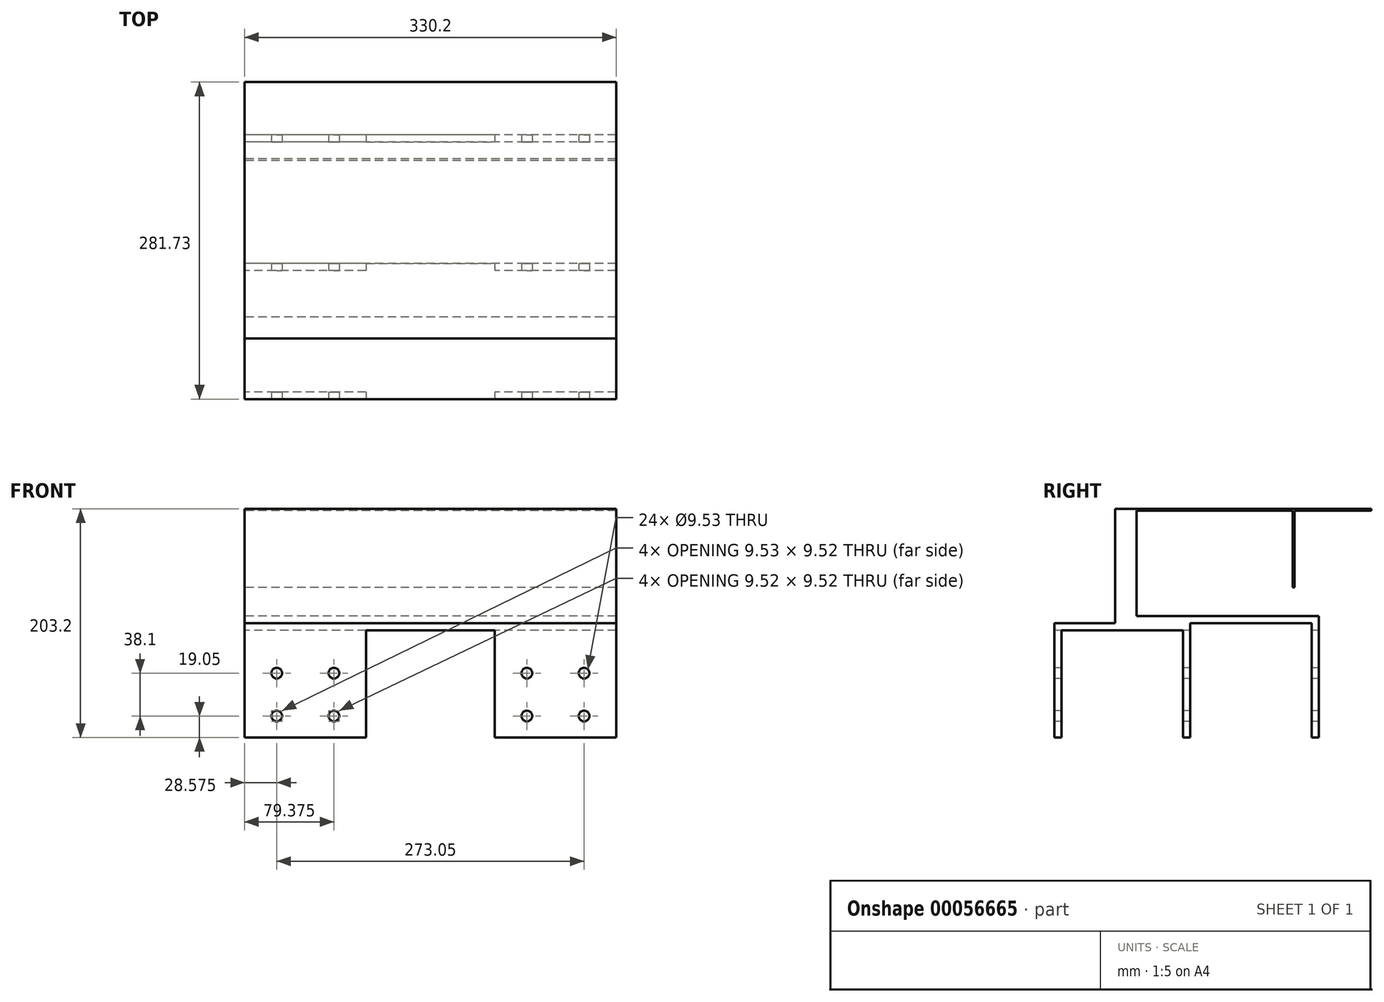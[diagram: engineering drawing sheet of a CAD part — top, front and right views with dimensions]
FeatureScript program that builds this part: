
annotation { "Feature Type Name" : "Feature", "Feature Type Description" : "" }
export const myFeature = defineFeature(function(context is Context, id is Id, definition is map)
    precondition{}
    {
        {
            var Q0;
            Q0=qCreatedBy(makeId("Right.planeOp"),FACE);
            var sketch = newSketch(context, id + "F0", { "sketchPlane" : qUnion([Q0])});
            skLineSegment(sketch, "E0", {"start": v(-73.02, -107.95) * mm, "end": v(-66.67, -107.95) * mm});
            skLineSegment(sketch, "E1", {"start": v(-66.67, -107.95) * mm, "end": v(-66.67, -12.7) * mm});
            skLineSegment(sketch, "E2", {"start": v(-66.67, -12.7) * mm, "end": v(-12.7, -12.7) * mm});
            skLineSegment(sketch, "E3", {"start": v(-12.7, -12.7) * mm, "end": v(-12.7, 95.25) * mm});
            skLineSegment(sketch, "E4", {"start": v(-73.02, -107.95) * mm, "end": v(-73.02, -6.35) * mm});
            skLineSegment(sketch, "E5", {"start": v(-12.7, 95.25) * mm, "end": v(-12.7, -12.7) * mm});
            skLineSegment(sketch, "E6", {"start": v(-12.7, -12.7) * mm, "end": v(41.28, -12.7) * mm});
            skLineSegment(sketch, "E7", {"start": v(41.28, -12.7) * mm, "end": v(41.28, -107.95) * mm});
            skLineSegment(sketch, "E8", {"start": v(41.28, -107.95) * mm, "end": v(47.63, -107.95) * mm});
            skLineSegment(sketch, "E9", {"start": v(47.63, -107.95) * mm, "end": v(47.63, -6.35) * mm});
            skLineSegment(sketch, "E10", {"start": v(47.63, -6.35) * mm, "end": v(-6.35, -6.35) * mm});
            skLineSegment(sketch, "E11", {"start": v(-6.35, -6.35) * mm, "end": v(-6.35, 95.25) * mm});
            skLineSegment(sketch, "E12", {"start": v(-6.35, 95.25) * mm, "end": v(-12.7, 95.25) * mm});
            skLineSegment(sketch, "E13", {"start": v(-19.05, 95.25) * mm, "end": v(-12.7, 95.25) * mm});
            skLineSegment(sketch, "E14", {"start": v(-73.02, -6.35) * mm, "end": v(-19.05, -6.35) * mm});
            skLineSegment(sketch, "E15", {"start": v(-19.05, -6.35) * mm, "end": v(-19.05, 95.25) * mm});
            skLineSegment(sketch, "E16", {"start": v(-6.35, 95.25) * mm, "end": v(0, 95.25) * mm});
            skLineSegment(sketch, "E17", {"start": v(0, 95.25) * mm, "end": v(0, 0) * mm});
            skLineSegment(sketch, "E18", {"start": v(0, 0) * mm, "end": v(161.93, 0) * mm});
            skLineSegment(sketch, "E19", {"start": v(161.93, 0) * mm, "end": v(161.93, -107.95) * mm});
            skLineSegment(sketch, "E20", {"start": v(161.93, -107.95) * mm, "end": v(155.58, -107.95) * mm});
            skLineSegment(sketch, "E21", {"start": v(155.58, -107.95) * mm, "end": v(155.58, -6.35) * mm});
            skLineSegment(sketch, "E22", {"start": v(155.58, -6.35) * mm, "end": v(47.63, -6.35) * mm});
            skLineSegment(sketch, "E23", {"start": v(138.85, 93.66) * mm, "end": v(138.85, 25.4) * mm});
            skLineSegment(sketch, "E24", {"start": v(138.85, 25.4) * mm, "end": v(140.44, 25.4) * mm});
            skLineSegment(sketch, "E25", {"start": v(140.44, 25.4) * mm, "end": v(140.44, 93.66) * mm});
            skLineSegment(sketch, "E26", {"start": v(140.44, 93.66) * mm, "end": v(208.7, 93.66) * mm});
            skLineSegment(sketch, "E27", {"start": v(208.7, 93.66) * mm, "end": v(208.7, 95.25) * mm});
            skLineSegment(sketch, "E28", {"start": v(208.7, 95.25) * mm, "end": v(138.85, 95.25) * mm});
            skLineSegment(sketch, "E29", {"start": v(0, 95.25) * mm, "end": v(138.85, 95.25) * mm});
            skLineSegment(sketch, "E30", {"start": v(138.85, 93.66) * mm, "end": v(0, 93.66) * mm});
            skSolve(sketch);
        }
        {
            var Q0;
            Q0 = qSketchRegion(id + "F0", true);
            extrude(context, id + "F1", {"entities" : qUnion([Q0]), "endBound" : BoundingType.SYMMETRIC, "depth" : 330.2 * mm});
        }
        {
            var Q0;
            Q0=makeQuery(id+"F1.opExtrude","SWEPT_FACE",FACE,{"disambiguationData":[OSD([sQuery(id+"F0.wireOp",EDGE,"E4")])]});
            var sketch = newSketch(context, id + "F2", { "sketchPlane" : qUnion([Q0])});
            skCircle(sketch, "E31", {"center": v(-136.53, -88.9) * mm, "radius": 4.76 * mm});
            skCircle(sketch, "E32", {"center": v(136.53, -88.9) * mm, "radius": 4.76 * mm});
            skCircle(sketch, "E33.0.1.0", {"center": v(136.53, -50.8) * mm, "radius": 4.76 * mm});
            skCircle(sketch, "E33.1.0.0", {"center": v(85.72, -88.9) * mm, "radius": 4.76 * mm});
            skCircle(sketch, "E33.1.1.0", {"center": v(85.72, -50.8) * mm, "radius": 4.76 * mm});
            skLineSegment(sketch, "E33.direction1", {"start": v(136.53, -88.9) * mm, "end": v(85.72, -88.9) * mm, "construction": true});
            skLineSegment(sketch, "E33.direction2", {"start": v(136.53, -88.9) * mm, "end": v(136.53, -50.8) * mm, "construction": true});
            skCircle(sketch, "E34.0.1.0", {"center": v(-136.53, -50.8) * mm, "radius": 4.76 * mm});
            skCircle(sketch, "E34.1.0.0", {"center": v(-85.72, -88.9) * mm, "radius": 4.76 * mm});
            skCircle(sketch, "E34.1.1.0", {"center": v(-85.72, -50.8) * mm, "radius": 4.76 * mm});
            skLineSegment(sketch, "E34.direction1", {"start": v(-136.53, -88.9) * mm, "end": v(-85.72, -88.9) * mm, "construction": true});
            skLineSegment(sketch, "E34.direction2", {"start": v(-136.53, -88.9) * mm, "end": v(-136.53, -50.8) * mm, "construction": true});
            skLineSegment(sketch, "E35.bottom", {"start": v(-57.15, -107.95) * mm, "end": v(57.15, -107.95) * mm});
            skLineSegment(sketch, "E35.top", {"start": v(-57.15, -12.7) * mm, "end": v(57.15, -12.7) * mm});
            skLineSegment(sketch, "E35.left", {"start": v(-57.15, -107.95) * mm, "end": v(-57.15, -12.7) * mm});
            skLineSegment(sketch, "E35.right", {"start": v(57.15, -107.95) * mm, "end": v(57.15, -12.7) * mm});
            skSolve(sketch);
        }
        {
            var Q0;
            Q0 = qSketchRegion(id + "F2", true);
            extrude(context, id + "F3", {"entities" : qUnion([Q0]), "operationType" : NewBodyOperationType.REMOVE, "endBound" : BoundingType.THROUGH_ALL, "oppositeDirection" : true, "depth" : 25.4 * mm});
        }
    });
